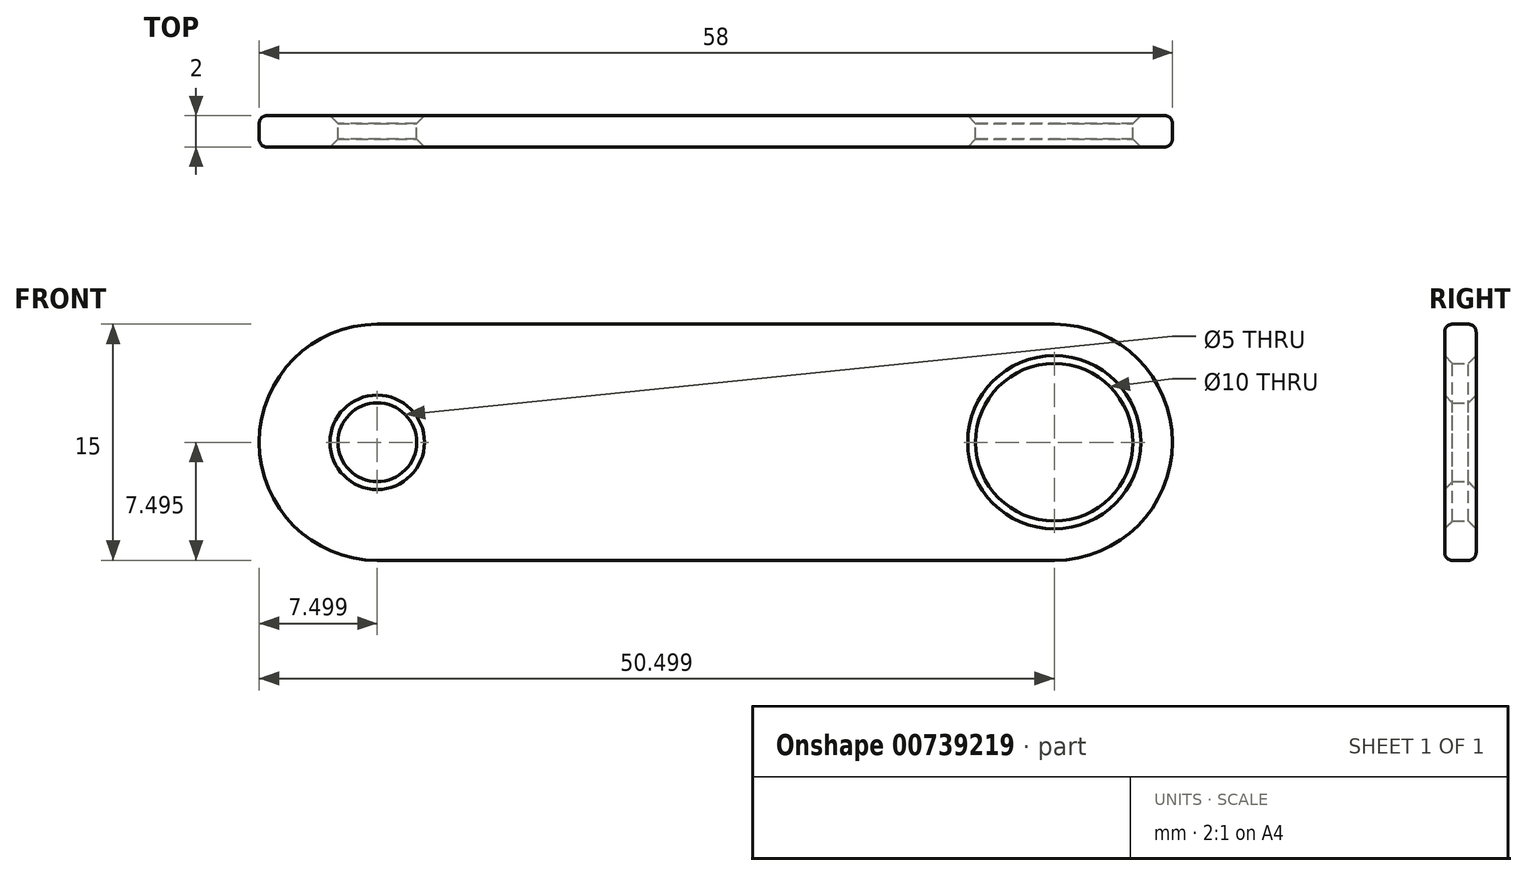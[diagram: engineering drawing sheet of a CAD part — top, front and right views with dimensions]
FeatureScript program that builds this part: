
annotation { "Feature Type Name" : "Feature", "Feature Type Description" : "" }
export const myFeature = defineFeature(function(context is Context, id is Id, definition is map)
    precondition{}
    {
        {
            var Q0;
            Q0=qCreatedBy(makeId("Front.planeOp"),FACE);
            var sketch = newSketch(context, id + "F0", { "sketchPlane" : qUnion([Q0])});
            skLineSegment(sketch, "E0", {"start": v(-32.02, 8.52) * mm, "end": v(10.98, 8.52) * mm});
            skLineSegment(sketch, "E1", {"start": v(10.98, -6.48) * mm, "end": v(-32.02, -6.48) * mm});
            skArc(sketch, "E2", {"start": v(-32.02, 8.52) * mm, "mid": v(-39.52, 1.02) * mm, "end": v(-32.02, -6.48) * mm});
            skArc(sketch, "E3", {"start": v(10.98, -6.48) * mm, "mid": v(18.48, 1.02) * mm, "end": v(10.98, 8.52) * mm});
            skCircle(sketch, "E4", {"center": v(-32.02, 1.02) * mm, "radius": 2.5 * mm});
            skCircle(sketch, "E5", {"center": v(10.98, 1.02) * mm, "radius": 5 * mm});
            skSolve(sketch);
        }
        {
            var Q0;
            Q0 = qSketchRegion(id + "F0", true);
            extrude(context, id + "F1", {"entities" : qUnion([Q0]), "depth" : 2 * mm, "offsetDistance" : 25.4 * mm});
        }
        {
            var Q0;
            Q0=makeQuery(id+"F1.opExtrude","CAP_EDGE",EDGE,{"disambiguationData":[OSD([sQuery(id+"F0.wireOp",EDGE,"E0")])],"isStart":false});
            var Q1;
            Q1=makeQuery(id+"F1.opExtrude","CAP_EDGE",EDGE,{"disambiguationData":[OSD([sQuery(id+"F0.wireOp",EDGE,"E2")])],"isStart":true});
            fillet(context, id + "F2", {"entities" : qUnion([Q0, Q1]), "radius" : 0.5 * mm, "tangentPropagation" : true, "allowEdgeOverflow" : false});
        }
        {
            var Q0;
            Q0=makeQuery(id+"F1.opExtrude","CAP_EDGE",EDGE,{"disambiguationData":[OSD([sQuery(id+"F0.wireOp",EDGE,"E4")])],"isStart":false});
            var Q1;
            Q1=makeQuery(id+"F1.opExtrude","CAP_EDGE",EDGE,{"disambiguationData":[OSD([sQuery(id+"F0.wireOp",EDGE,"E5")])],"isStart":false});
            var Q2;
            Q2=makeQuery(id+"F1.opExtrude","CAP_EDGE",EDGE,{"disambiguationData":[OSD([sQuery(id+"F0.wireOp",EDGE,"E4")])],"isStart":true});
            var Q3;
            Q3=makeQuery(id+"F1.opExtrude","CAP_EDGE",EDGE,{"disambiguationData":[OSD([sQuery(id+"F0.wireOp",EDGE,"E5")])],"isStart":true});
            chamfer(context, id + "F3", {"entities" : qUnion([Q0, Q1, Q2, Q3]), "width" : 0.5 * mm, "tangentPropagation" : true});
        }
    });
